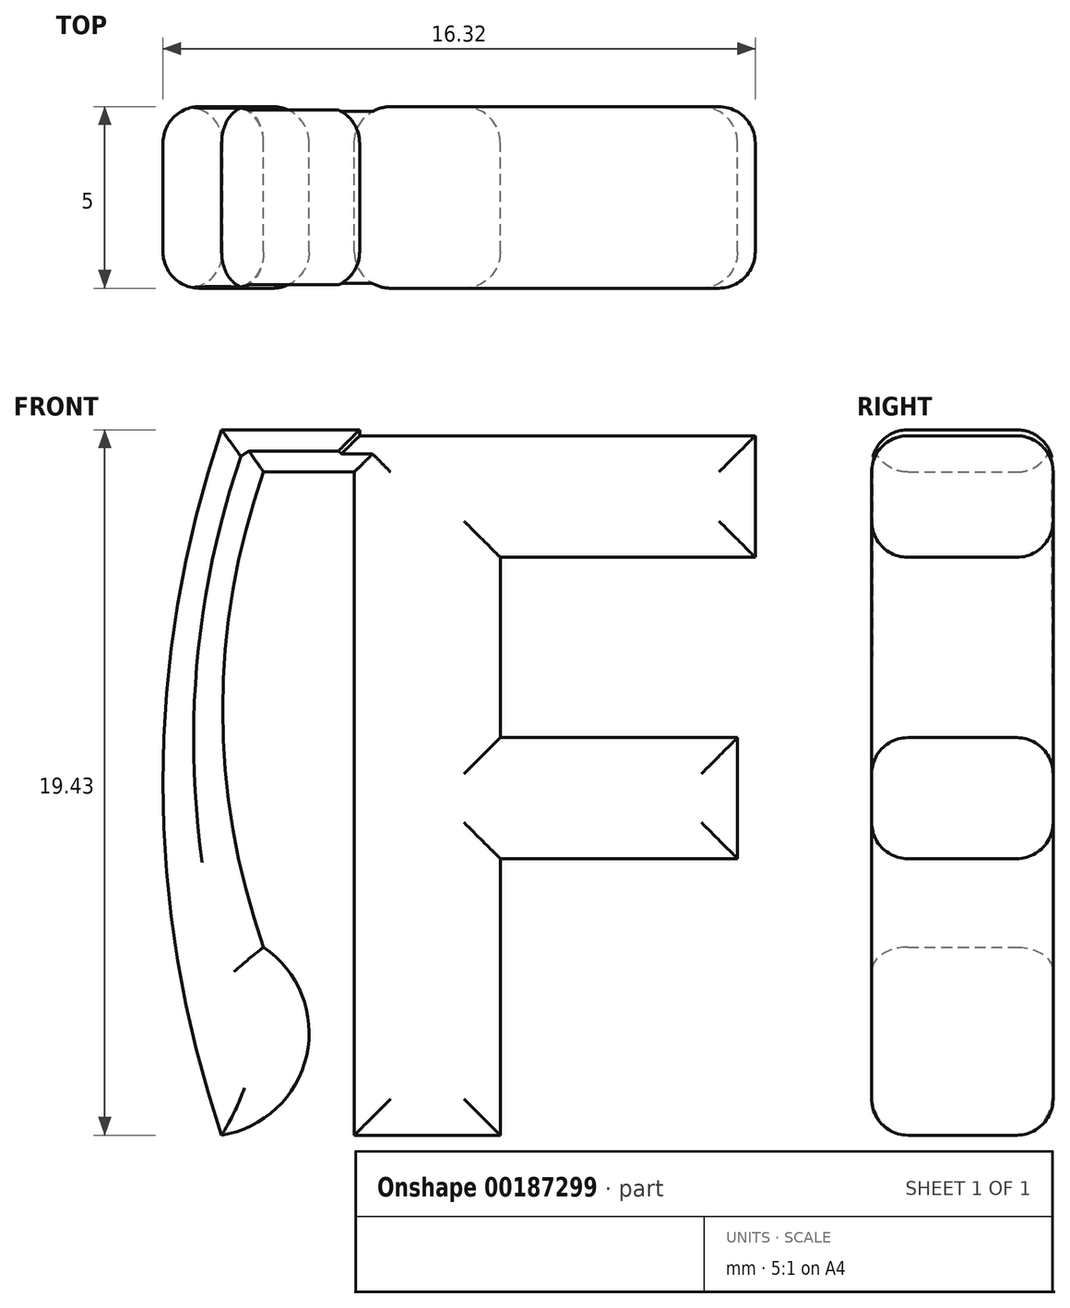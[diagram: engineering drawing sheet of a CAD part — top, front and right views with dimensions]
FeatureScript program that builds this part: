
annotation { "Feature Type Name" : "Feature", "Feature Type Description" : "" }
export const myFeature = defineFeature(function(context is Context, id is Id, definition is map)
    precondition{}
    {
        {
            var Q0;
            Q0=qCreatedBy(makeId("Front.planeOp"),FACE);
            var sketch = newSketch(context, id + "F0", { "sketchPlane" : qUnion([Q0])});
            skLineSegment(sketch, "E0", {"start": v(0, 19.43) * mm, "end": v(3.8, 19.43) * mm});
            skLineSegment(sketch, "E1", {"start": v(3.8, 19.43) * mm, "end": v(3.8, 18.27) * mm});
            skLineSegment(sketch, "E2", {"start": v(3.8, 18.27) * mm, "end": v(1.16, 18.27) * mm});
            skArc(sketch, "E3", {"start": v(0, 0) * mm, "mid": v(2.34, 2.2) * mm, "end": v(1.16, 5.18) * mm});
            skText(sketch, "E4", { "text": "F", "fontName": "OpenSans-Bold.ttf"});
            skArc(sketch, "E5", {"start": v(1.16, 18.27) * mm, "mid": v(0.03, 11.72) * mm, "end": v(1.16, 5.18) * mm});
            skArc(sketch, "E6", {"start": v(0, 19.43) * mm, "mid": v(-1.62, 9.71) * mm, "end": v(0, 0) * mm});
            const initialGuessF0  = {"E4": [0.00123, 0, 1, 0, 0.01943]};
            skSetInitialGuess(sketch, initialGuessF0);
            skSolve(sketch);
        }
        {
            var Q0;
            Q0 = qSketchRegion(id + "F0", true);
            extrude(context, id + "F1", {"entities" : qUnion([Q0]), "depth" : 5 * mm});
        }
        {
            var Q0;
            Q0=makeQuery(id+"F1.opExtrude","CAP_FACE",FACE,{"disambiguationData":[OSD([sQuery(id+"F0.wireOp",EDGE,"be7xAEPO-sKVT-0Ak3-rtqd-BYsUKJHZuXb5"),sQuery(id+"F0.wireOp",EDGE,"E0"),sQuery(id+"F0.wireOp",EDGE,"E1"),sQuery(id+"F0.wireOp",EDGE,"E2"),sQuery(id+"F0.wireOp",EDGE,"7xSTVDnR-abPq-wSY4-ofMi-LYckJfvl9Wuv"),sQuery(id+"F0.wireOp",EDGE,"E3"),sQuery(id+"F0.wireOp",EDGE,"E4.sketch_text.stroke-0"),sQuery(id+"F0.wireOp",EDGE,"E4.sketch_text.stroke-1"),sQuery(id+"F0.wireOp",EDGE,"E4.sketch_text.stroke-2"),sQuery(id+"F0.wireOp",EDGE,"E4.sketch_text.stroke-3"),sQuery(id+"F0.wireOp",EDGE,"E4.sketch_text.stroke-4"),sQuery(id+"F0.wireOp",EDGE,"E4.sketch_text.stroke-5"),sQuery(id+"F0.wireOp",EDGE,"E4.sketch_text.stroke-6"),sQuery(id+"F0.wireOp",EDGE,"E4.sketch_text.stroke-7"),sQuery(id+"F0.wireOp",EDGE,"E4.sketch_text.stroke-8"),sQuery(id+"F0.wireOp",EDGE,"E4.sketch_text.stroke-9")])],"isStart":false});
            var Q1;
            Q1=makeQuery(id+"F1.opExtrude","CAP_FACE",FACE,{"disambiguationData":[OSD([sQuery(id+"F0.wireOp",EDGE,"be7xAEPO-sKVT-0Ak3-rtqd-BYsUKJHZuXb5"),sQuery(id+"F0.wireOp",EDGE,"E0"),sQuery(id+"F0.wireOp",EDGE,"E1"),sQuery(id+"F0.wireOp",EDGE,"E2"),sQuery(id+"F0.wireOp",EDGE,"7xSTVDnR-abPq-wSY4-ofMi-LYckJfvl9Wuv"),sQuery(id+"F0.wireOp",EDGE,"E3"),sQuery(id+"F0.wireOp",EDGE,"E4.sketch_text.stroke-0"),sQuery(id+"F0.wireOp",EDGE,"E4.sketch_text.stroke-1"),sQuery(id+"F0.wireOp",EDGE,"E4.sketch_text.stroke-2"),sQuery(id+"F0.wireOp",EDGE,"E4.sketch_text.stroke-3"),sQuery(id+"F0.wireOp",EDGE,"E4.sketch_text.stroke-4"),sQuery(id+"F0.wireOp",EDGE,"E4.sketch_text.stroke-5"),sQuery(id+"F0.wireOp",EDGE,"E4.sketch_text.stroke-6"),sQuery(id+"F0.wireOp",EDGE,"E4.sketch_text.stroke-7"),sQuery(id+"F0.wireOp",EDGE,"E4.sketch_text.stroke-8"),sQuery(id+"F0.wireOp",EDGE,"E4.sketch_text.stroke-9")])],"isStart":true});
            fillet(context, id + "F2", {"entities" : qUnion([Q0, Q1]), "radius" : 1 * mm, "tangentPropagation" : true, "allowEdgeOverflow" : false});
        }
    });
